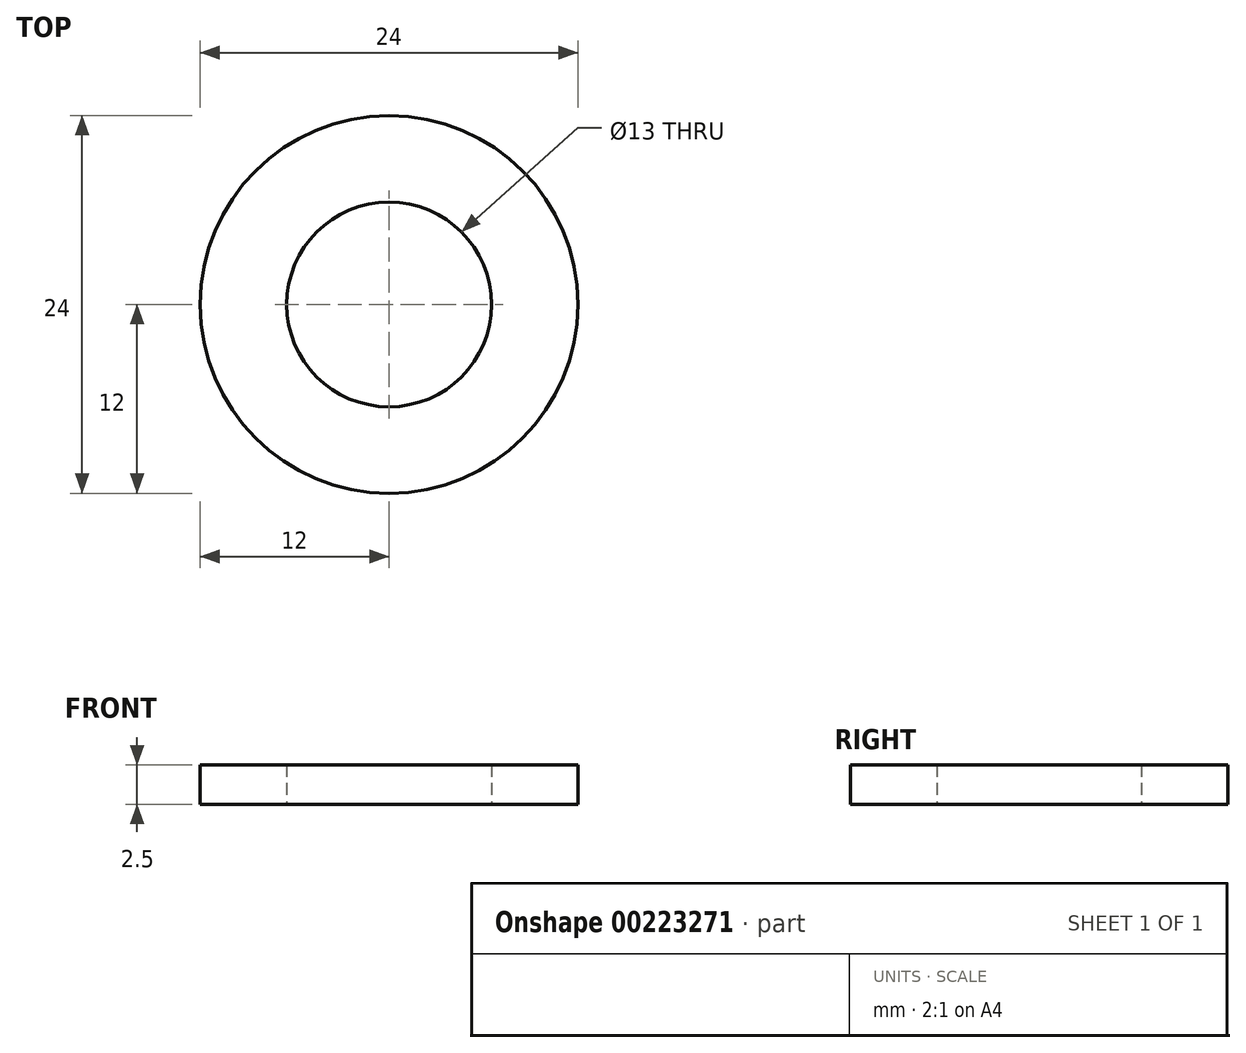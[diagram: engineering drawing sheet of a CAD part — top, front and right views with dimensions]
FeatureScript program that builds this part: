
annotation { "Feature Type Name" : "Feature", "Feature Type Description" : "" }
export const myFeature = defineFeature(function(context is Context, id is Id, definition is map)
    precondition{}
    {
        {
            var Q0;
            Q0=qCreatedBy(makeId("Top.planeOp"),FACE);
            var sketch = newSketch(context, id + "F0", { "sketchPlane" : qUnion([Q0])});
            skCircle(sketch, "E0", {"center": v(0, 0) * mm, "radius": 12 * mm});
            skCircle(sketch, "E1", {"center": v(0, 0) * mm, "radius": 6.5 * mm});
            skSolve(sketch);
        }
        {
            var Q0;
            Q0 = qSketchRegion(id + "F0", true);
            extrude(context, id + "F1", {"entities" : qUnion([Q0]), "depth" : 2.5 * mm});
        }
    });
